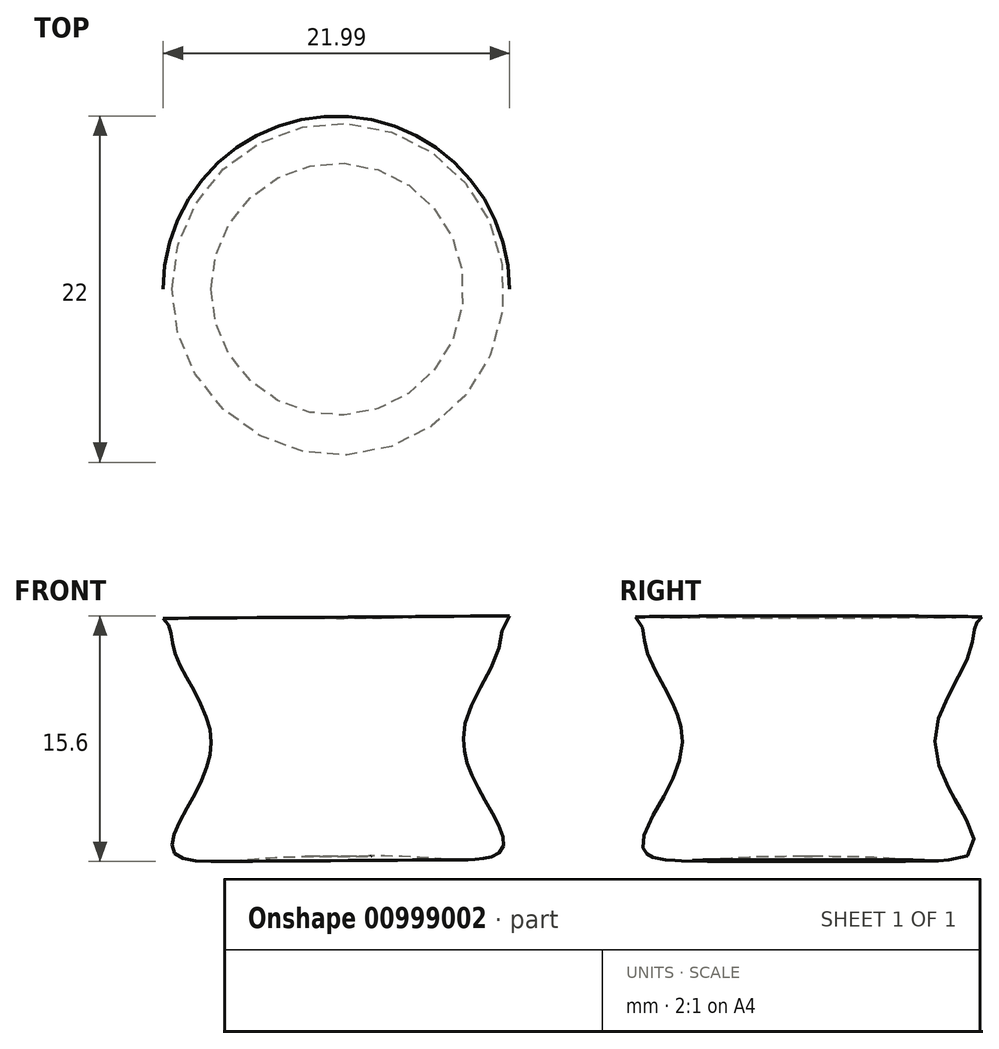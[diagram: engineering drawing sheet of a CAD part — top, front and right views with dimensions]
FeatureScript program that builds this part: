
annotation { "Feature Type Name" : "Feature", "Feature Type Description" : "" }
export const myFeature = defineFeature(function(context is Context, id is Id, definition is map)
    precondition{}
    {
        {
            var Q0;
            Q0=qCreatedBy(makeId("Front.planeOp"),FACE);
            var sketch = newSketch(context, id + "F0", { "sketchPlane" : qUnion([Q0])});
            skFitSpline(sketch, "E0", {"points": [v(-41.84, 42.68) * mm, v(-41.14, 40.66) * mm, v(-39, 36.12) * mm, v(-39.67, 31.83) * mm, v(-41.15, 27.81) * mm, v(-35.93, 27.42) * mm, v(-30.74, 27.55) * mm], "startDerivative": vector(15.63, -11.87) * mm, "endDerivative": vector(38.93, 0) * mm});
            skLineSegment(sketch, "E1", {"start": v(-41.84, 42.68) * mm, "end": v(-30.84, 42.68) * mm});
            skLineSegment(sketch, "E2", {"start": v(-30.84, 42.68) * mm, "end": v(-30.74, 27.55) * mm});
            skSolve(sketch);
        }
        {
            var Q0;
            Q0 = qSketchRegion(id + "F0", true);
            var Q1;
            Q1=sQuery(id+"F0.wireOp",EDGE,"E2");
            revolve(context, id + "F1", {"surfaceOperationType" : NewSurfaceOperationType.NEW, "entities" : qUnion([Q0]), "axis" : qUnion([Q1]), "revolveType" : RevolveType.FULL});
        }
    });
